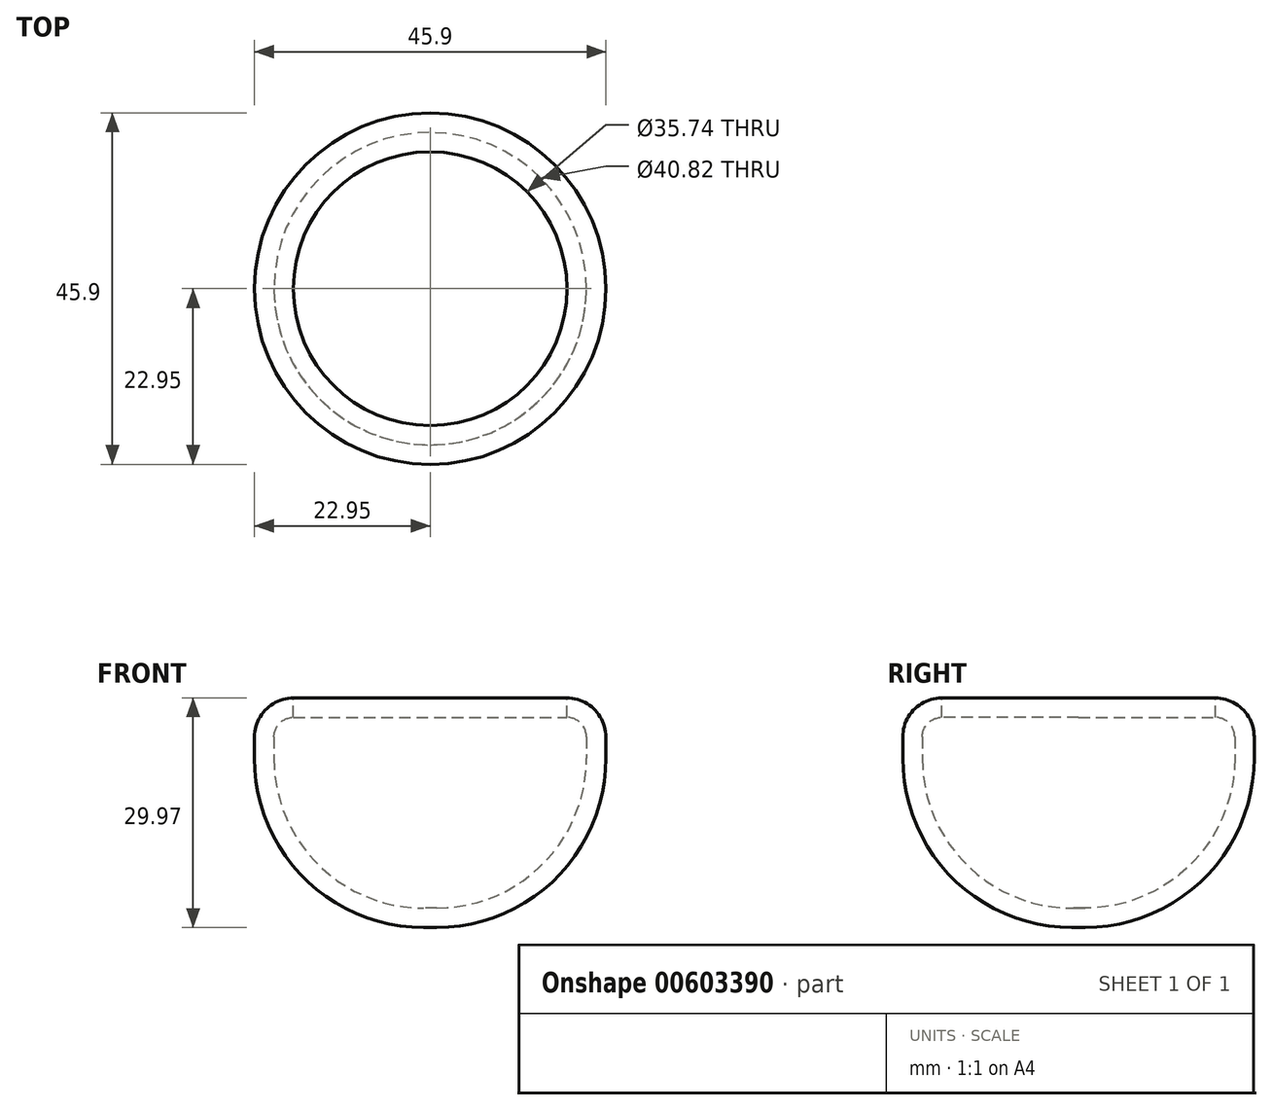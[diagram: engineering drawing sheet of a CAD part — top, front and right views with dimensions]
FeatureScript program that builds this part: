
annotation { "Feature Type Name" : "Feature", "Feature Type Description" : "" }
export const myFeature = defineFeature(function(context is Context, id is Id, definition is map)
    precondition{}
    {
        {
            var Q0;
            Q0=qCreatedBy(makeId("Top.planeOp"),FACE);
            var sketch = newSketch(context, id + "F0", { "sketchPlane" : qUnion([Q0])});
            skCircle(sketch, "E0", {"center": v(0, 0) * mm, "radius": 22.95 * mm});
            skSolve(sketch);
        }
        {
            var Q0;
            Q0=makeQuery(id+"F0.imprint","IMPRINT",FACE,{"disambiguationData":[TD([[makeQuery(id+"F0.imprint","IMPRINT",EDGE,{"derivedFrom":sQuery(id+"F0.wireOp",EDGE,"E0")}),1.0]])]});
            extrude(context, id + "F1", {"entities" : qUnion([Q0]), "depth" : 29.97 * mm, "offsetDistance" : 25.4 * mm});
        }
        {
            var Q0;
            Q0=makeQuery(id+"F1.opExtrude","CAP_EDGE",EDGE,{"disambiguationData":[OSD([sQuery(id+"F0.wireOp",EDGE,"E0")])],"isStart":false});
            fillet(context, id + "F2", {"entities" : qUnion([Q0]), "radius" : 5.08 * mm, "tangentPropagation" : true, "allowEdgeOverflow" : false});
        }
        {
            var Q0;
            Q0=makeQuery(id+"F1.opExtrude","CAP_EDGE",EDGE,{"disambiguationData":[OSD([sQuery(id+"F0.wireOp",EDGE,"E0")])],"isStart":true});
            fillet(context, id + "F3", {"entities" : qUnion([Q0]), "radius" : 22.08 * mm, "tangentPropagation" : true, "allowEdgeOverflow" : false});
        }
        {
            var Q0;
            Q0=makeQuery(id+"F1.opExtrude","CAP_FACE",FACE,{"disambiguationData":[OSD([sQuery(id+"F0.wireOp",EDGE,"E0")])],"isStart":false});
            shell(context, id + "F4", {"entities" : qUnion([Q0]), "thickness" : 2.54 * mm});
        }
    });
